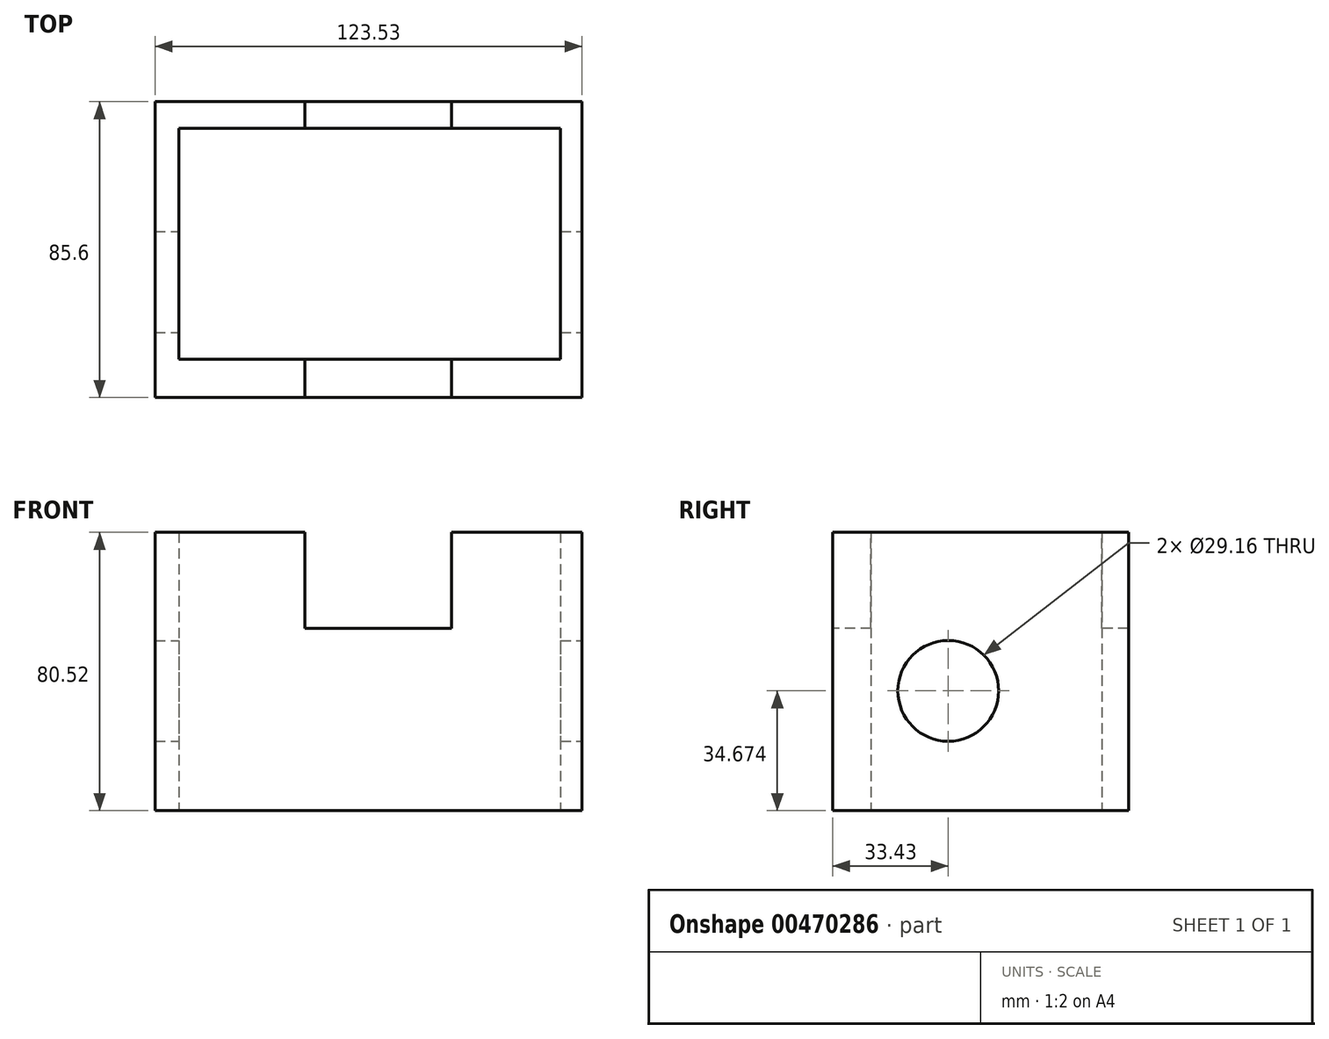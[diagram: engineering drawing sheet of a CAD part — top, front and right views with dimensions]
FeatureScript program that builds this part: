
annotation { "Feature Type Name" : "Feature", "Feature Type Description" : "" }
export const myFeature = defineFeature(function(context is Context, id is Id, definition is map)
    precondition{}
    {
        {
            var Q0;
            Q0=qCreatedBy(makeId("Top.planeOp"),FACE);
            var sketch = newSketch(context, id + "F0", { "sketchPlane" : qUnion([Q0])});
            skLineSegment(sketch, "E0.bottom", {"start": v(-62.33, -33.43) * mm, "end": v(61.2, -33.43) * mm});
            skLineSegment(sketch, "E0.top", {"start": v(-62.33, 52.17) * mm, "end": v(61.2, 52.17) * mm});
            skLineSegment(sketch, "E0.left", {"start": v(-62.33, -33.43) * mm, "end": v(-62.33, 52.17) * mm});
            skLineSegment(sketch, "E0.right", {"start": v(61.2, -33.43) * mm, "end": v(61.2, 52.17) * mm});
            skLineSegment(sketch, "E1.bottom", {"start": v(-55.47, -22.33) * mm, "end": v(54.94, -22.33) * mm});
            skLineSegment(sketch, "E1.top", {"start": v(-55.47, 44.47) * mm, "end": v(54.94, 44.47) * mm});
            skLineSegment(sketch, "E1.left", {"start": v(-55.47, -22.33) * mm, "end": v(-55.47, 44.47) * mm});
            skLineSegment(sketch, "E1.right", {"start": v(54.94, -22.33) * mm, "end": v(54.94, 44.47) * mm});
            skSolve(sketch);
        }
        {
            var Q0;
            Q0=makeQuery(id+"F0.imprint","IMPRINT",FACE,{"disambiguationData":[TD([[makeQuery(id+"F0.imprint","IMPRINT",EDGE,{"derivedFrom":sQuery(id+"F0.wireOp",EDGE,"E0.bottom")}),1.0]])]});
            extrude(context, id + "F1", {"entities" : qUnion([Q0]), "depth" : 80.52 * mm});
        }
        {
            var Q0;
            Q0=makeQuery(id+"F1.opExtrude","SWEPT_FACE",FACE,{"disambiguationData":[OSD([sQuery(id+"F0.wireOp",EDGE,"E0.bottom")])]});
            var sketch = newSketch(context, id + "F2", { "sketchPlane" : qUnion([Q0])});
            skLineSegment(sketch, "E2.bottom", {"start": v(-18.96, 80.52) * mm, "end": v(23.39, 80.52) * mm});
            skLineSegment(sketch, "E2.top", {"start": v(-18.96, 52.8) * mm, "end": v(23.39, 52.8) * mm});
            skLineSegment(sketch, "E2.left", {"start": v(-18.96, 80.52) * mm, "end": v(-18.96, 52.8) * mm});
            skLineSegment(sketch, "E2.right", {"start": v(23.39, 80.52) * mm, "end": v(23.39, 52.8) * mm});
            skSolve(sketch);
        }
        {
            var Q0;
            Q0=makeQuery(id+"F2.imprint","IMPRINT",FACE,{"disambiguationData":[TD([[makeQuery(id+"F2.imprint","IMPRINT",EDGE,{"derivedFrom":sQuery(id+"F2.wireOp",EDGE,"E2.bottom")}),-1.0]])]});
            extrude(context, id + "F3", {"entities" : qUnion([Q0]), "operationType" : NewBodyOperationType.REMOVE, "endBound" : BoundingType.THROUGH_ALL, "oppositeDirection" : true, "depth" : 25.4 * mm});
        }
        {
            var Q0;
            Q0=makeQuery(id+"F1.opExtrude","SWEPT_FACE",FACE,{"disambiguationData":[OSD([sQuery(id+"F0.wireOp",EDGE,"E0.right")])]});
            var sketch = newSketch(context, id + "F4", { "sketchPlane" : qUnion([Q0])});
            skCircle(sketch, "E3", {"center": v(0, 34.67) * mm, "radius": 14.58 * mm});
            skSolve(sketch);
        }
        {
            var Q0;
            Q0=makeQuery(id+"F4.imprint","IMPRINT",FACE,{"disambiguationData":[TD([[makeQuery(id+"F4.imprint","IMPRINT",EDGE,{"derivedFrom":sQuery(id+"F4.wireOp",EDGE,"E3")}),1.0]])]});
            extrude(context, id + "F5", {"entities" : qUnion([Q0]), "operationType" : NewBodyOperationType.REMOVE, "endBound" : BoundingType.THROUGH_ALL, "oppositeDirection" : true, "depth" : 25.4 * mm});
        }
    });
